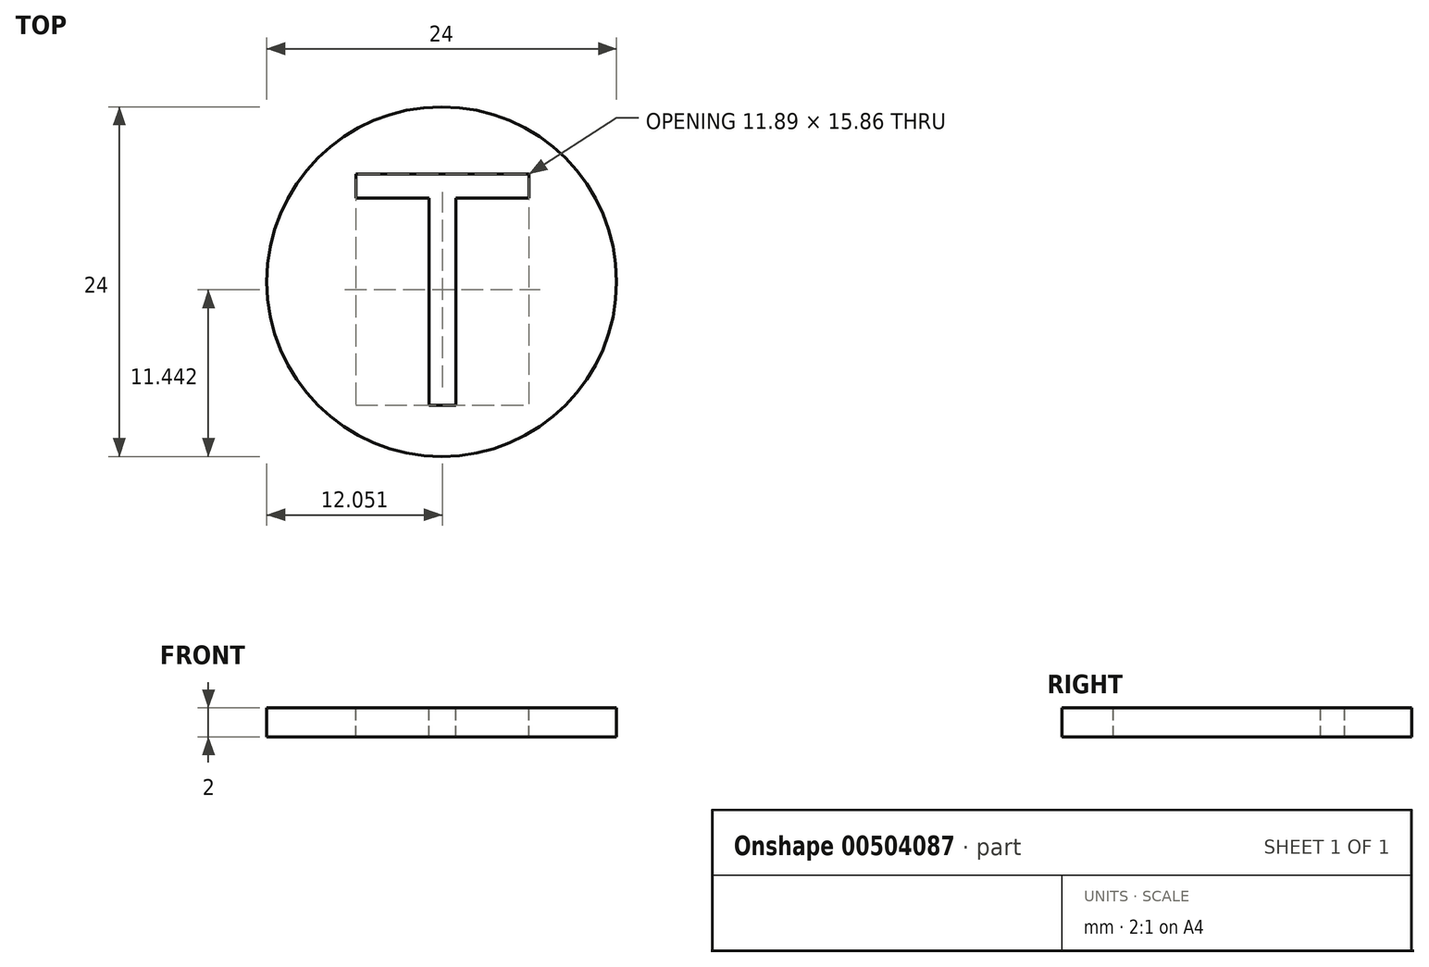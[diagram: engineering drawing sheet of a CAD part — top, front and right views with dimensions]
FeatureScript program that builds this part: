
annotation { "Feature Type Name" : "Feature", "Feature Type Description" : "" }
export const myFeature = defineFeature(function(context is Context, id is Id, definition is map)
    precondition{}
    {
        {
            var Q0;
            Q0=qCreatedBy(makeId("Top.planeOp"),FACE);
            var sketch = newSketch(context, id + "F0", { "sketchPlane" : qUnion([Q0])});
            skCircle(sketch, "E0", {"center": v(0, 0) * mm, "radius": 12 * mm});
            skSolve(sketch);
        }
        {
            var Q0;
            Q0=qSketchRegion(id+"F0",true);
            extrude(context, id + "F1", {"entities" : qUnion([Q0]), "depth" : 2 * mm});
        }
        {
            var Q0;
            Q0=makeQuery(id+"F1.opExtrude","CAP_FACE",FACE,{"disambiguationData":[OSD([sQuery(id+"F0.wireOp",EDGE,"E0")])],"isStart":false});
            var sketch = newSketch(context, id + "F2", { "sketchPlane" : qUnion([Q0])});
            skText(sketch, "E1", { "text": "T", "fontName": "OpenSans-Regular.ttf"});
            const initialGuessF2  = {"E1": [-0.00609, -0.00849, 1, 0, 0.016]};
            skSetInitialGuess(sketch, initialGuessF2);
            skSolve(sketch);
        }
        {
            var Q0;
            Q0 = qSketchRegion(id + "F2", true);
            extrude(context, id + "F3", {"entities" : qUnion([Q0]), "operationType" : NewBodyOperationType.REMOVE, "oppositeDirection" : true, "depth" : 25 * mm, "offsetDistance" : 25 * mm});
        }
    });
